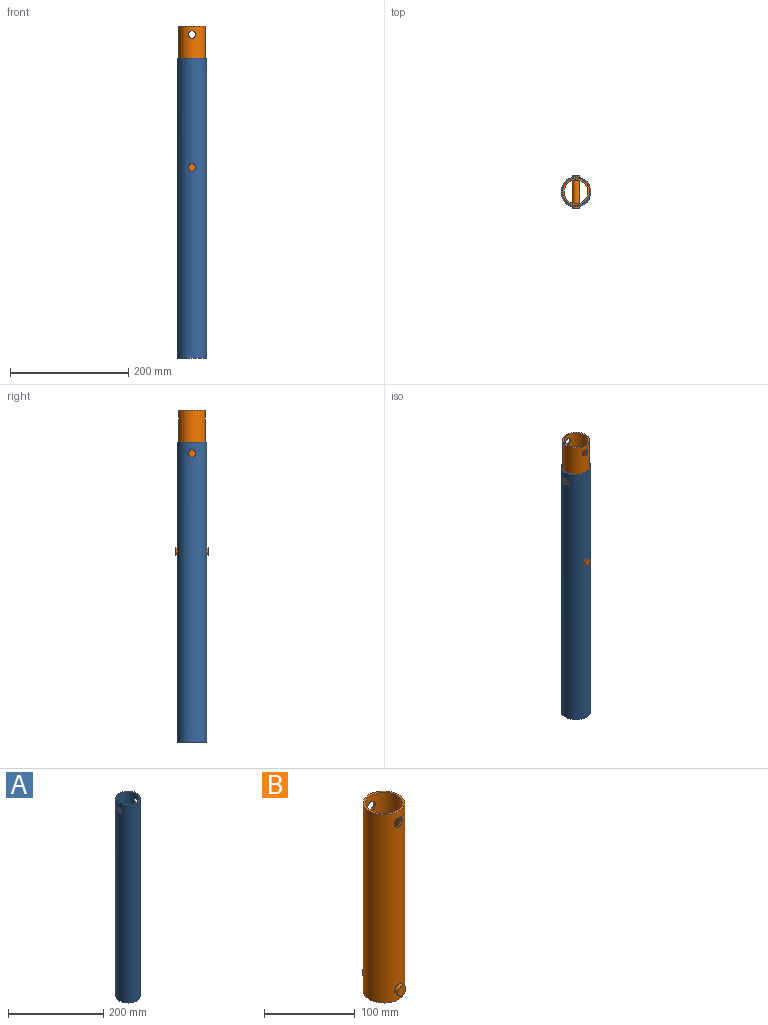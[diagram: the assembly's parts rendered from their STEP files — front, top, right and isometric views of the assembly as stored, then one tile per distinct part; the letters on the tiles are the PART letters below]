
ASSEMBLY  parts=2 mates=1
PART A: 6 faces, bbox 50.8x50.8x508 mm
  f0: cylinder r=22.86mm len=508mm, axis (0,0,-1), area 72709.8mm2, adj f2,f3,f4,f5
  f1: cylinder r=25.4mm len=508mm, axis (0,0,-1), area 80818mm2, adj f2,f3,f4,f5
  f2: plane 50.8x50.8mm, normal (0,0,1), area 385.1mm2, adj f0,f1
  f3: plane 50.8x50.8mm, normal (0,0,-1), area 385.1mm2, adj f0,f1
  f4: cylinder r=6.35mm len=12.7mm, axis (1,0,0), area 103.2mm2, adj f0,f1
  f5: cylinder r=6.35mm len=12.7mm, axis (-1,0,0), area 103.2mm2, adj f0,f1
PART B: 11 faces, bbox 45.7x55.9x254 mm
  f0: cylinder r=20.32mm len=254mm, axis (0,0,-1), area 31916.2mm2, adj f2,f3,f4,f5,f8
  f1: cylinder r=22.86mm len=254mm, axis (0,0,-1), area 35971.1mm2, adj f2,f3,f4,f5,f7,f10
  f2: plane 45.72x45.72mm, normal (0,0,1), area 344.6mm2, adj f0,f1
  f3: plane 45.72x45.72mm, normal (0,0,-1), area 344.6mm2, adj f0,f1
  f4: cylinder r=6.35mm len=12.7mm, axis (0,-1,0), area 103.6mm2, adj f0,f1
  f5: cylinder r=6.35mm len=12.7mm, axis (0,1,0), area 103.7mm2, adj f0,f1
  f6: plane 12.7x12.7mm, normal (0,-1,0), area 126.7mm2, adj f7
  f7: cylinder r=6.35mm len=12.7mm, axis (0,1,0), area 220.5mm2, adj f1,f6
  f8: cylinder r=6.35mm len=40.64mm, axis (0,1,0), area 1581.1mm2, adj f0
  f9: plane 12.7x12.7mm, normal (0,1,0), area 126.7mm2, adj f10
  f10: cylinder r=6.35mm len=12.7mm, axis (0,-1,0), area 220.6mm2, adj f1,f9
PLACE A t=(-316.55,-8.68,-134.35)mm
PLACE B t=(-316.55,-8.68,174.29)mm
MATE slider B.f1 <-> A.f0  axis (0,0,-1) through (-316.55,-8.68,301.29)mm
